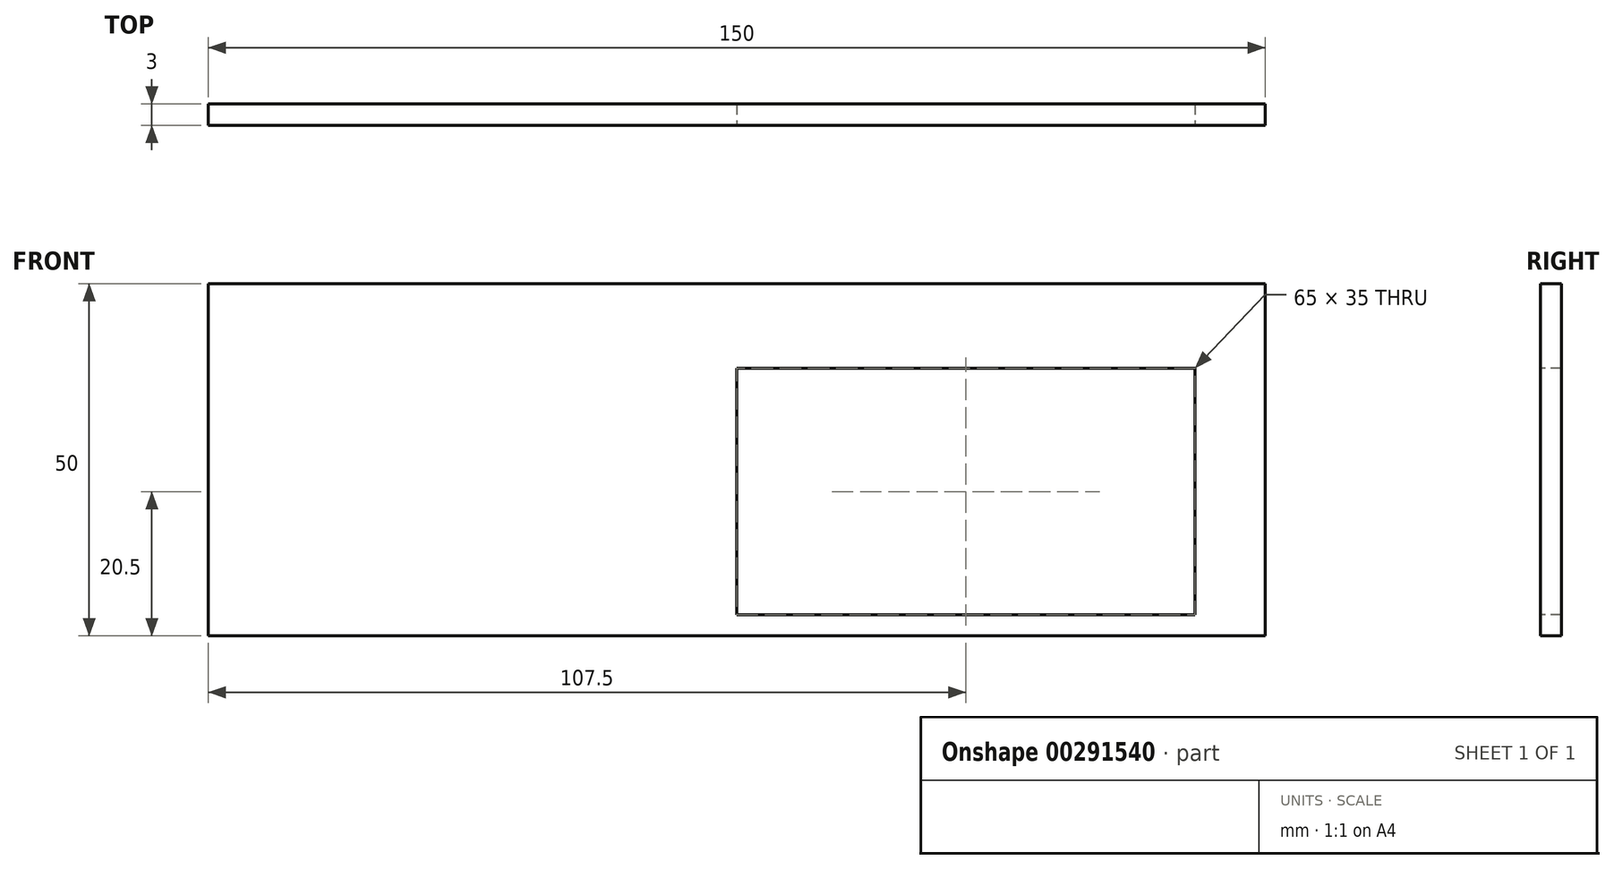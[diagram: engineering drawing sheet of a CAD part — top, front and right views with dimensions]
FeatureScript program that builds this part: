
annotation { "Feature Type Name" : "Feature", "Feature Type Description" : "" }
export const myFeature = defineFeature(function(context is Context, id is Id, definition is map)
    precondition{}
    {
        {
            var Q0;
            Q0=qCreatedBy(makeId("Front.planeOp"),FACE);
            var sketch = newSketch(context, id + "F0", { "sketchPlane" : qUnion([Q0])});
            skLineSegment(sketch, "E0.bottom", {"start": v(-75, 25) * mm, "end": v(75, 25) * mm});
            skLineSegment(sketch, "E0.top", {"start": v(-75, -25) * mm, "end": v(75, -25) * mm});
            skLineSegment(sketch, "E0.left", {"start": v(-75, 25) * mm, "end": v(-75, -25) * mm});
            skLineSegment(sketch, "E0.right", {"start": v(75, 25) * mm, "end": v(75, -25) * mm});
            skSolve(sketch);
        }
        {
            var Q0;
            Q0=makeQuery(id+"F0.imprint","IMPRINT",FACE,{"disambiguationData":[TD([[makeQuery(id+"F0.imprint","IMPRINT",EDGE,{"derivedFrom":sQuery(id+"F0.wireOp",EDGE,"E0.bottom")}),-1.0]])]});
            extrude(context, id + "F1", {"entities" : qUnion([Q0]), "endBound" : BoundingType.SYMMETRIC, "depth" : 3 * mm});
        }
        {
            var Q0;
            Q0=makeQuery(id+"F1.opExtrude","CAP_FACE",FACE,{"disambiguationData":[OSD([sQuery(id+"F0.wireOp",EDGE,"E0.bottom"),sQuery(id+"F0.wireOp",EDGE,"E0.top"),sQuery(id+"F0.wireOp",EDGE,"E0.left"),sQuery(id+"F0.wireOp",EDGE,"E0.right")])],"isStart":false});
            var sketch = newSketch(context, id + "F2", { "sketchPlane" : qUnion([Q0])});
            skLineSegment(sketch, "E1.bottom", {"start": v(0, 13) * mm, "end": v(65, 13) * mm});
            skLineSegment(sketch, "E1.top", {"start": v(0, -22) * mm, "end": v(65, -22) * mm});
            skLineSegment(sketch, "E1.left", {"start": v(0, 13) * mm, "end": v(0, -22) * mm});
            skLineSegment(sketch, "E1.right", {"start": v(65, 13) * mm, "end": v(65, -22) * mm});
            skSolve(sketch);
        }
        {
            var Q0;
            Q0=qSketchRegion(id+"F2",true);
            extrude(context, id + "F3", {"entities" : qUnion([Q0]), "operationType" : NewBodyOperationType.REMOVE, "endBound" : BoundingType.UP_TO_NEXT, "oppositeDirection" : true, "depth" : 25 * mm});
        }
    });
